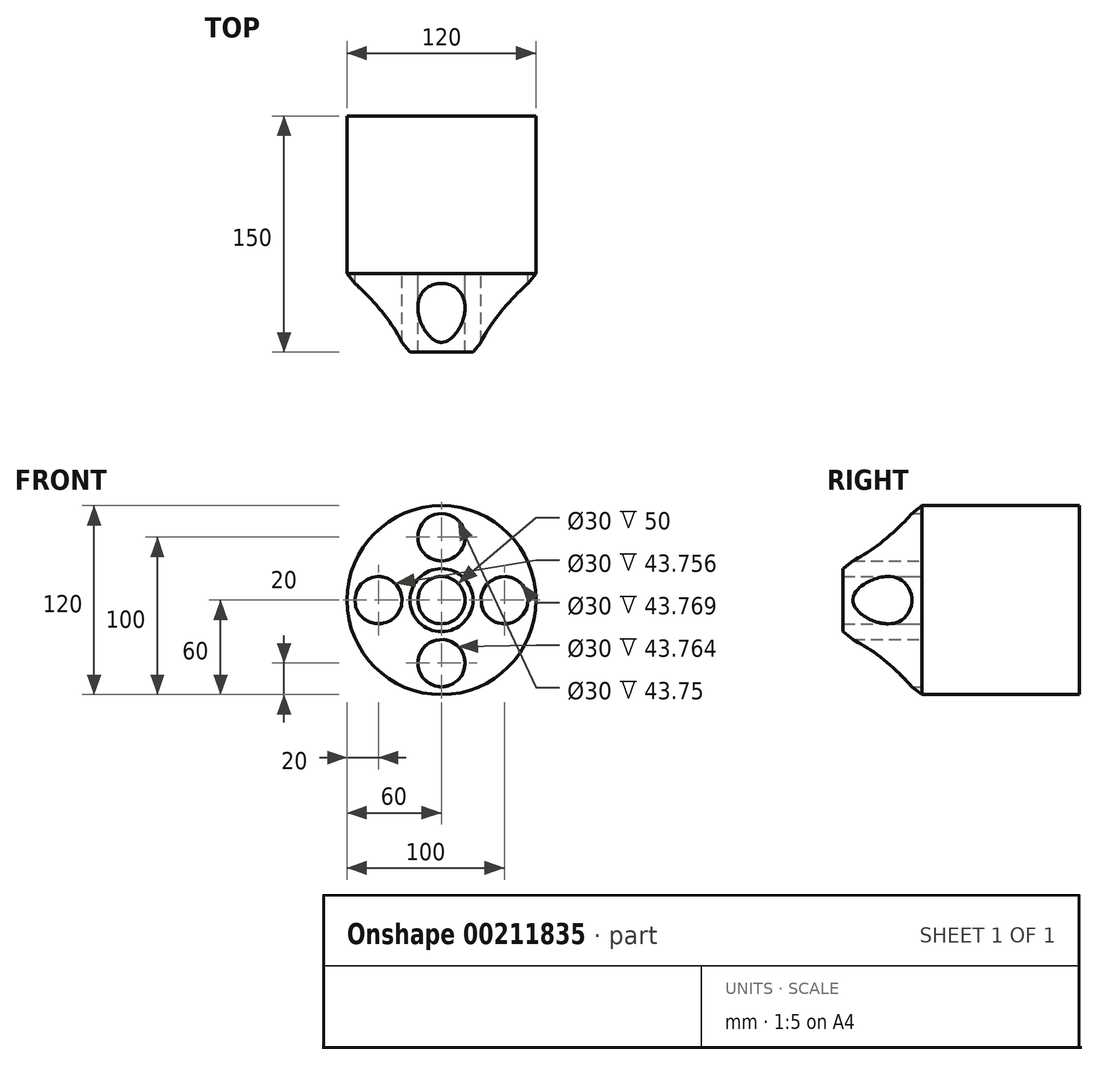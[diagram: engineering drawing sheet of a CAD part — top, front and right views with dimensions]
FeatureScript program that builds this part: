
annotation { "Feature Type Name" : "Feature", "Feature Type Description" : "" }
export const myFeature = defineFeature(function(context is Context, id is Id, definition is map)
    precondition{}
    {
        {
            var Q0;
            Q0=qCreatedBy(makeId("Top.planeOp"),FACE);
            var sketch = newSketch(context, id + "F3", { "sketchPlane" : qUnion([Q0])});
            skLineSegment(sketch, "E0", {"start": v(-60, 0) * mm, "end": v(-20, -50) * mm});
            skLineSegment(sketch, "E1", {"start": v(-20, -50) * mm, "end": v(0, -50) * mm});
            skLineSegment(sketch, "E2", {"start": v(0, 0) * mm, "end": v(0, -50) * mm});
            skLineSegment(sketch, "E3", {"start": v(0, 0) * mm, "end": v(-60, 0) * mm});
            skLineSegment(sketch, "E4", {"start": v(-20, -50) * mm, "end": v(-20, 0) * mm, "construction": true});
            skSolve(sketch);
        }
        {
            var Q0;
            Q0=makeQuery(id+"F3.imprint","IMPRINT",FACE,{"disambiguationData":[TD([[makeQuery(id+"F3.imprint","IMPRINT",EDGE,{"derivedFrom":sQuery(id+"F3.wireOp",EDGE,"E0")}),1.0]])]});
            var Q1;
            Q1=sQuery(id+"F3.wireOp",EDGE,"E2");
            revolve(context, id + "F0", {"entities" : qUnion([Q0]), "axis" : qUnion([Q1]), "revolveType" : RevolveType.FULL});
        }
        {
            var Q0;
            Q0=makeQuery(id+"F0.opRevolve","SWEPT_FACE",FACE,{"disambiguationData":[OSD([sQuery(id+"F3.wireOp",EDGE,"E3")])]});
            extrude(context, id + "F4", {"entities" : qUnion([Q0]), "operationType" : NewBodyOperationType.ADD, "depth" : 100 * mm});
        }
        {
            var Q0;
            Q0=qCreatedBy(makeId("Front.planeOp"),FACE);
            var sketch = newSketch(context, id + "F1", { "sketchPlane" : qUnion([Q0])});
            skCircle(sketch, "E5", {"center": v(0, 0) * mm, "radius": 15 * mm});
            skCircle(sketch, "E6", {"center": v(0, 40) * mm, "radius": 15 * mm});
            skLineSegment(sketch, "E7", {"start": v(-64.68, 0) * mm, "end": v(67.34, 0) * mm, "construction": true});
            skLineSegment(sketch, "E8", {"start": v(34.1, -34.1) * mm, "end": v(0, 0) * mm, "construction": true});
            skCircle(sketch, "E9.MirrorC", {"center": v(0, -40) * mm, "radius": 15 * mm});
            skLineSegment(sketch, "E10.MirrorCS", {"start": v(34.1, 34.1) * mm, "end": v(0, 0) * mm, "construction": true});
            skCircle(sketch, "E11.MirrorC", {"center": v(40, 0) * mm, "radius": 15 * mm});
            skCircle(sketch, "E12.MirrorC", {"center": v(-40, 0) * mm, "radius": 15 * mm});
            skSolve(sketch);
        }
        {
            var Q0;
            Q0 = qSketchRegion(id + "F1", true);
            extrude(context, id + "F2", {"entities" : qUnion([Q0]), "operationType" : NewBodyOperationType.REMOVE, "endBound" : BoundingType.THROUGH_ALL, "depth" : 25 * mm});
        }
    });
